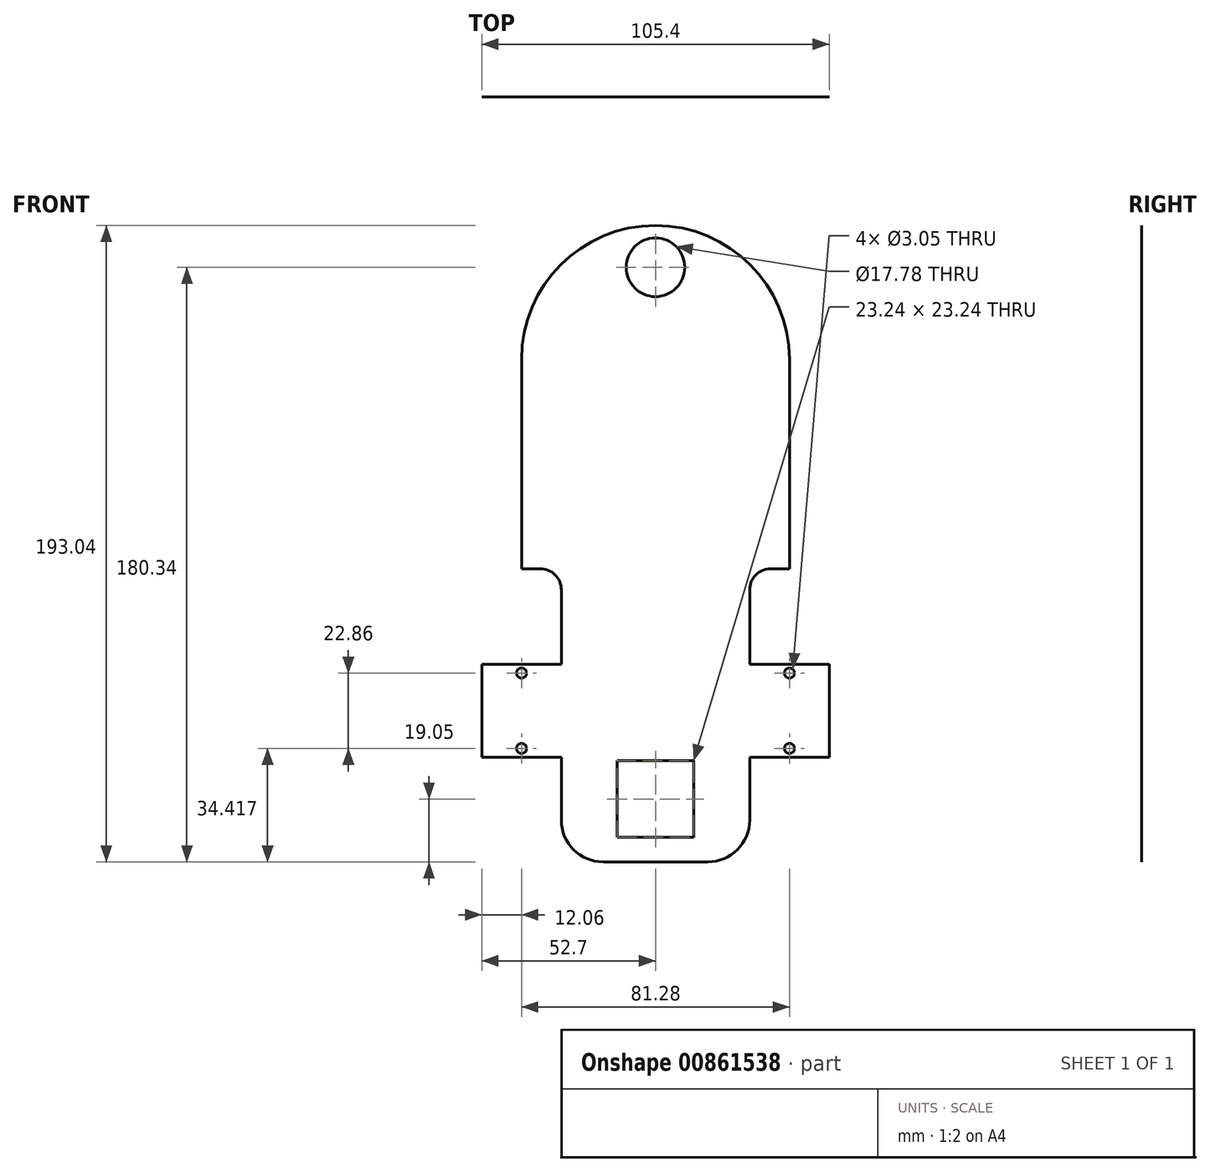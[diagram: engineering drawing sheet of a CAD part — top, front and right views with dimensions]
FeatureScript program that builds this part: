
annotation { "Feature Type Name" : "Feature", "Feature Type Description" : "" }
export const myFeature = defineFeature(function(context is Context, id is Id, definition is map)
    precondition{}
    {
        {
            var Q0;
            Q0=qCreatedBy(makeId("Front.planeOp"),FACE);
            var sketch = newSketch(context, id + "F0", { "sketchPlane" : qUnion([Q0])});
            skLineSegment(sketch, "E0.bottom", {"start": v(40.64, -31.75) * mm, "end": v(34.92, -31.75) * mm});
            skLineSegment(sketch, "E0.left", {"start": v(40.64, -31.75) * mm, "end": v(40.64, 31.75) * mm});
            skLineSegment(sketch, "E0.right", {"start": v(-40.64, -31.75) * mm, "end": v(-40.64, 31.75) * mm});
            skPoint(sketch, "E0.middle", {"position": v(0, 0) * mm});
            skLineSegment(sketch, "E1.top", {"start": v(15.88, -120.65) * mm, "end": v(-15.88, -120.65) * mm});
            skLineSegment(sketch, "E1.left", {"start": v(28.57, -38.1) * mm, "end": v(28.57, -60.7) * mm});
            skLineSegment(sketch, "E1.right", {"start": v(-28.58, -38.1) * mm, "end": v(-28.58, -60.7) * mm});
            skPoint(sketch, "E1.middle", {"position": v(0, -76.2) * mm});
            skLineSegment(sketch, "E2.trimOffspring", {"start": v(-34.93, -31.75) * mm, "end": v(-40.64, -31.75) * mm});
            skPoint(sketch, "E3.visualSharp", {"position": v(28.57, -31.75) * mm});
            skArc(sketch, "E3.filletArc", {"start": v(34.92, -31.75) * mm, "mid": v(30.43, -33.6) * mm, "end": v(28.57, -38.1) * mm});
            skPoint(sketch, "E4.visualSharp", {"position": v(-28.58, -31.75) * mm});
            skArc(sketch, "E4.filletArc", {"start": v(-28.58, -38.1) * mm, "mid": v(-30.43, -33.6) * mm, "end": v(-34.93, -31.75) * mm});
            skPoint(sketch, "E5.visualSharp", {"position": v(28.58, -120.65) * mm});
            skArc(sketch, "E5.filletArc", {"start": v(15.88, -120.65) * mm, "mid": v(24.86, -116.93) * mm, "end": v(28.58, -107.95) * mm});
            skPoint(sketch, "E6.visualSharp", {"position": v(-28.57, -120.65) * mm});
            skArc(sketch, "E6.filletArc", {"start": v(-28.58, -107.95) * mm, "mid": v(-24.86, -116.93) * mm, "end": v(-15.88, -120.65) * mm});
            skArc(sketch, "E7", {"start": v(40.64, 31.75) * mm, "mid": v(0, 72.4) * mm, "end": v(-40.64, 31.75) * mm});
            skLineSegment(sketch, "E8.bottom", {"start": v(11.62, -113.22) * mm, "end": v(-11.62, -113.22) * mm});
            skLineSegment(sketch, "E8.top", {"start": v(11.62, -89.98) * mm, "end": v(-11.62, -89.98) * mm});
            skLineSegment(sketch, "E8.left", {"start": v(11.62, -113.22) * mm, "end": v(11.62, -89.98) * mm});
            skLineSegment(sketch, "E8.right", {"start": v(-11.62, -113.22) * mm, "end": v(-11.62, -89.98) * mm});
            skPoint(sketch, "E8.middle", {"position": v(0, -101.6) * mm});
            skPoint(sketch, "E9.middle", {"position": v(0, -50.41) * mm});
            skCircle(sketch, "E10", {"center": v(0, 59.7) * mm, "radius": 8.9 * mm});
            skLineSegment(sketch, "E11.bottom", {"start": v(28.57, -60.7) * mm, "end": v(52.7, -60.7) * mm});
            skLineSegment(sketch, "E11.top", {"start": v(28.57, -88.9) * mm, "end": v(52.7, -88.9) * mm});
            skLineSegment(sketch, "E11.right", {"start": v(52.7, -60.7) * mm, "end": v(52.7, -88.9) * mm});
            skLineSegment(sketch, "E12.trimOffspring", {"start": v(28.57, -88.9) * mm, "end": v(28.58, -107.95) * mm});
            skLineSegment(sketch, "E13.MirrorCS", {"start": v(-28.57, -60.7) * mm, "end": v(-52.7, -60.7) * mm});
            skLineSegment(sketch, "E14.MirrorCS", {"start": v(-52.7, -60.7) * mm, "end": v(-52.7, -88.9) * mm});
            skLineSegment(sketch, "E15.MirrorCS", {"start": v(-28.57, -88.9) * mm, "end": v(-52.7, -88.9) * mm});
            skLineSegment(sketch, "E16.trimOffspring", {"start": v(-28.58, -88.9) * mm, "end": v(-28.58, -107.95) * mm});
            skCircle(sketch, "E17", {"center": v(40.64, -63.37) * mm, "radius": 1.52 * mm});
            skCircle(sketch, "E18", {"center": v(40.64, -86.23) * mm, "radius": 1.52 * mm});
            skCircle(sketch, "E19.MirrorC", {"center": v(-40.64, -63.37) * mm, "radius": 1.52 * mm});
            skCircle(sketch, "E20.MirrorC", {"center": v(-40.64, -86.23) * mm, "radius": 1.52 * mm});
            skSolve(sketch);
        }
        {
            var Q0;
            Q0 = qSketchRegion(id + "F0", true);
            extrude(context, id + "F1", {"entities" : qUnion([Q0]), "depth" : 1 / 203.2 * mm, "offsetDistance" : 25.4 * mm, "symmetric" : true});
        }
    });
